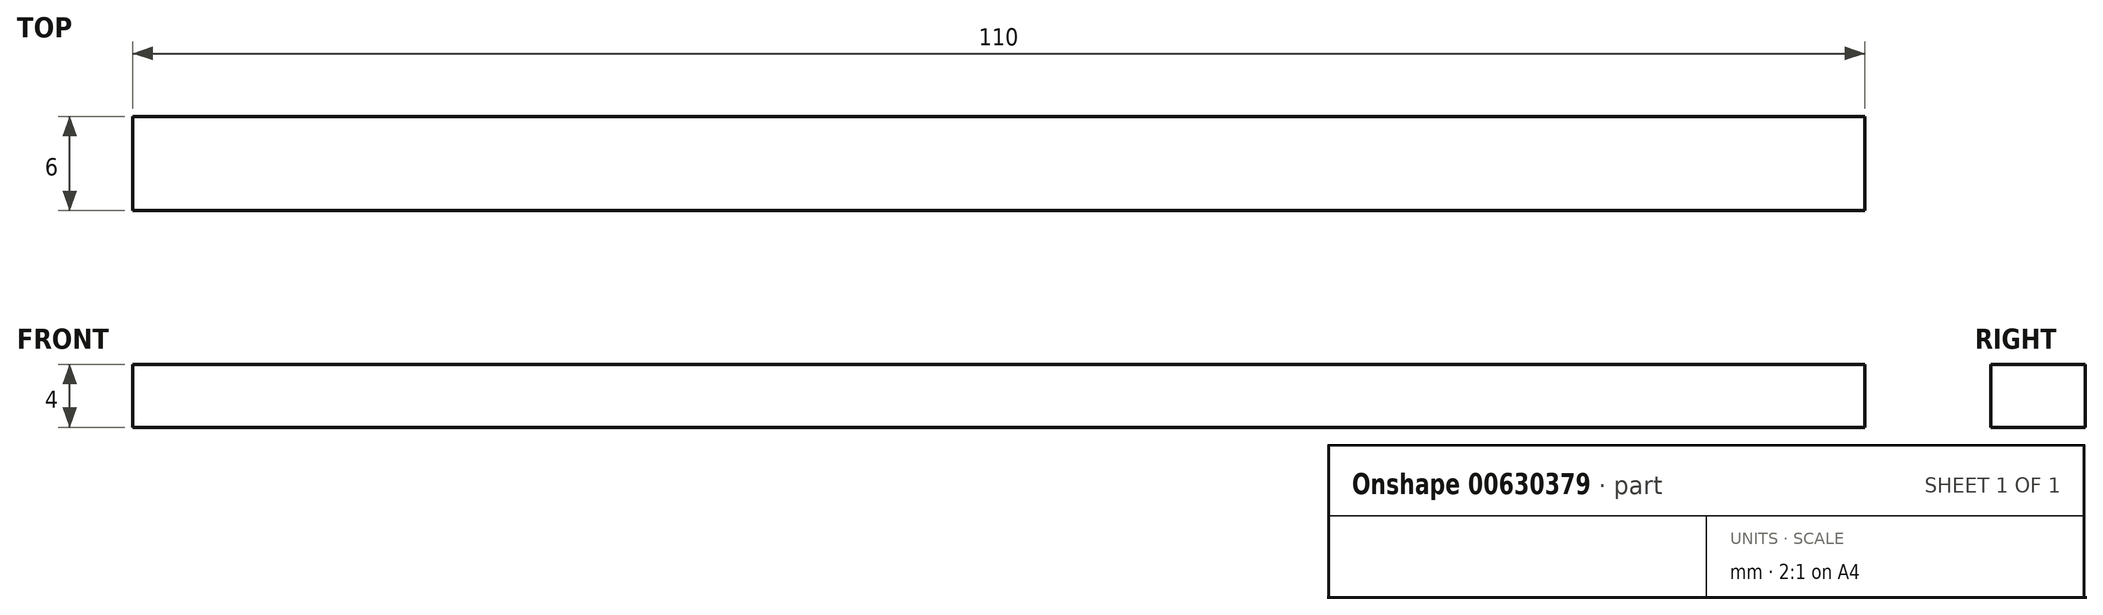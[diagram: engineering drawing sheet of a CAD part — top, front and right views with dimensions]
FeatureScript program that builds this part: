
annotation { "Feature Type Name" : "Feature", "Feature Type Description" : "" }
export const myFeature = defineFeature(function(context is Context, id is Id, definition is map)
    precondition{}
    {
        {
            var Q0;
            Q0=qCreatedBy(makeId("Top.planeOp"),FACE);
            var sketch = newSketch(context, id + "F0", { "sketchPlane" : qUnion([Q0])});
            skLineSegment(sketch, "E0.bottom", {"start": v(0, 0) * mm, "end": v(110, 0) * mm});
            skLineSegment(sketch, "E0.top", {"start": v(0, 6) * mm, "end": v(110, 6) * mm});
            skLineSegment(sketch, "E0.left", {"start": v(0, 0) * mm, "end": v(0, 6) * mm});
            skLineSegment(sketch, "E0.right", {"start": v(110, 0) * mm, "end": v(110, 6) * mm});
            skSolve(sketch);
        }
        {
            var Q0;
            Q0 = qSketchRegion(id + "F0", true);
            extrude(context, id + "F1", {"entities" : qUnion([Q0]), "depth" : 4 * mm, "offsetDistance" : 25 * mm});
        }
    });
